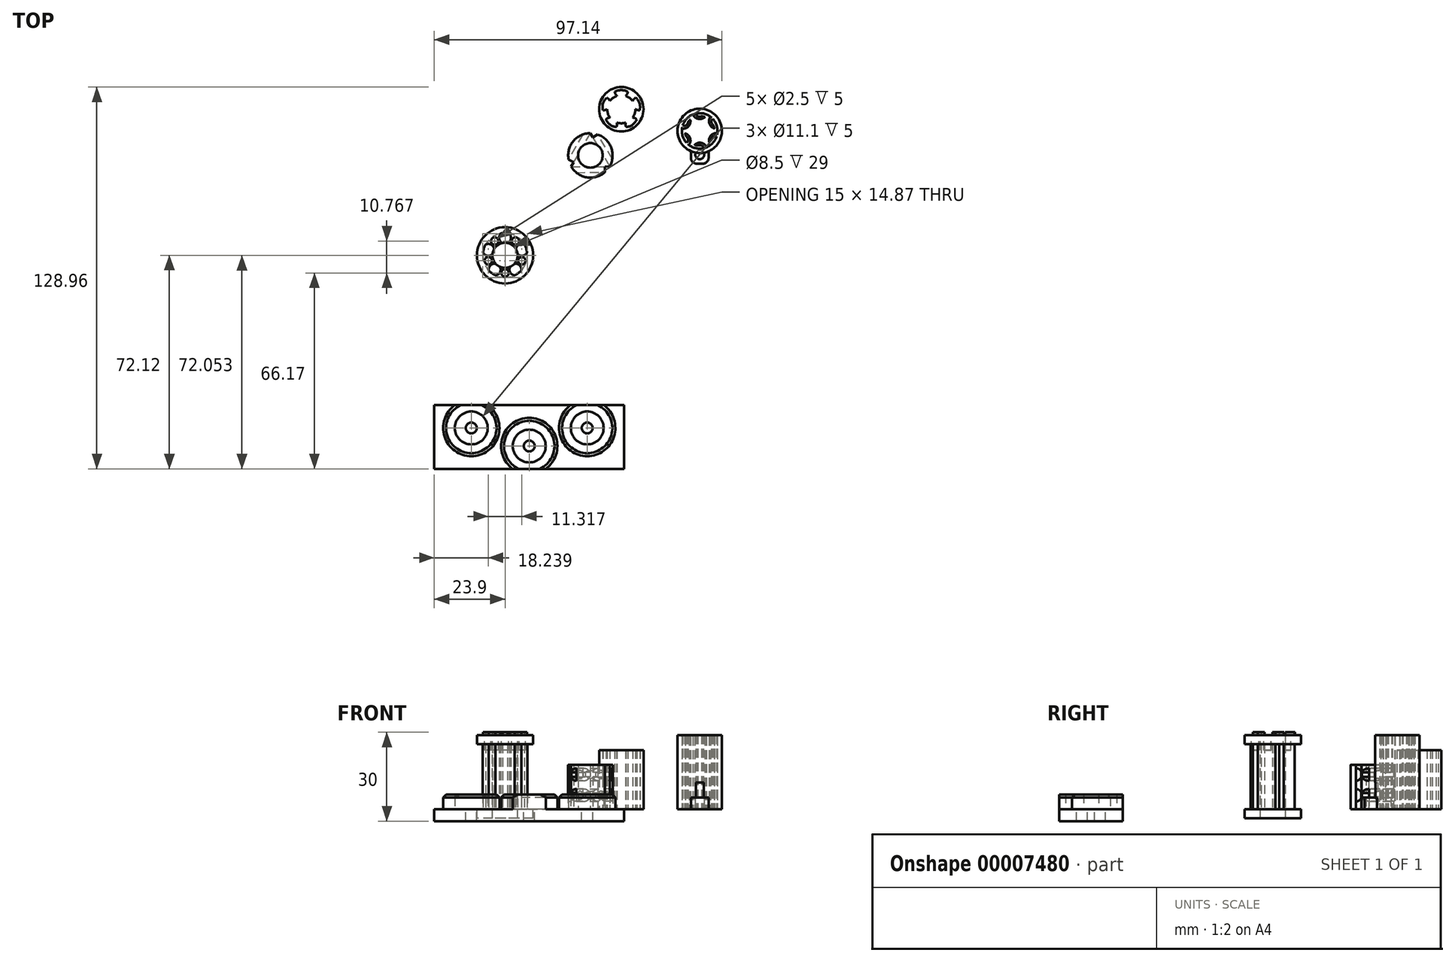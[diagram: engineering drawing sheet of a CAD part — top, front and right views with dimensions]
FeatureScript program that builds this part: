
annotation { "Feature Type Name" : "Feature", "Feature Type Description" : "" }
export const myFeature = defineFeature(function(context is Context, id is Id, definition is map)
    precondition{}
    {
        {
            var Q0;
            Q0=qCreatedBy(makeId("Top.planeOp"),FACE);
            var sketch = newSketch(context, id + "F0", { "sketchPlane" : qUnion([Q0])});
            skCircle(sketch, "E0", {"center": v(0, 0) * mm, "radius": 7.5 * mm});
            skCircle(sketch, "E1", {"center": v(0, 0) * mm, "radius": 3.95 * mm, "construction": true});
            skLineSegment(sketch, "E2", {"start": v(0, 3.95) * mm, "end": v(0, 7.5) * mm, "construction": true});
            skCircle(sketch, "E3", {"center": v(0, 5.95) * mm, "radius": 2 * mm});
            skCircle(sketch, "E4", {"center": v(0, 0) * mm, "radius": 4.25 * mm});
            skCircle(sketch, "E5", {"center": v(0, 0) * mm, "radius": 9.5 * mm});
            skCircle(sketch, "E6.1.0", {"center": v(-5.66, 1.84) * mm, "radius": 2 * mm});
            skCircle(sketch, "E6.2.0", {"center": v(-3.5, -4.81) * mm, "radius": 2 * mm});
            skCircle(sketch, "E6.3.0", {"center": v(3.5, -4.81) * mm, "radius": 2 * mm});
            skCircle(sketch, "E6.4.0", {"center": v(5.66, 1.84) * mm, "radius": 2 * mm});
            skSolve(sketch);
        }
        {
            var Q0;
            Q0=makeQuery(id+"F0.imprint","IMPRINT",FACE,{"disambiguationData":[TD([[makeQuery(id+"F0.imprint","IMPRINT",EDGE,{"derivedFrom":sQuery(id+"F0.wireOp",EDGE,"E5")}),1.0]])]});
            var Q1;
            {var subQ0=sQuery(id+"F0.wireOp",EDGE,"E6.4.0");var subQ3=sQuery(id+"F0.wireOp",EDGE,"E0");var subQ6=makeQuery(id+"F0.imprint","INTERSECT",VERTEX,{"disambiguationData":[OD(0.0)],"derivedFrom":[subQ3,subQ0]});Q1=makeQuery(id+"F0.imprint","IMPRINT",FACE,{"disambiguationData":[TD([[makeQuery(id+"F0.imprint","IMPRINT",EDGE,{"disambiguationData":[TD([[subQ6,1.0]])],"derivedFrom":subQ3}),1.0]])]});}
            var Q2;
            {var subQ3=sQuery(id+"F0.wireOp",EDGE,"E0");var subQ5=sQuery(id+"F0.wireOp",EDGE,"E6.1.0");var subQ7=makeQuery(id+"F0.imprint","INTERSECT",VERTEX,{"disambiguationData":[OD(1.0)],"derivedFrom":[subQ3,subQ5]});Q2=makeQuery(id+"F0.imprint","IMPRINT",FACE,{"disambiguationData":[TD([[makeQuery(id+"F0.imprint","IMPRINT",EDGE,{"disambiguationData":[TD([[subQ7,-1.0]])],"derivedFrom":subQ3}),1.0]])]});}
            var Q3;
            {var subQ3=sQuery(id+"F0.wireOp",EDGE,"E0");var subQ5=sQuery(id+"F0.wireOp",EDGE,"E3");var subQ7=makeQuery(id+"F0.imprint","INTERSECT",VERTEX,{"disambiguationData":[OD(1.0)],"derivedFrom":[subQ3,subQ5]});Q3=makeQuery(id+"F0.imprint","IMPRINT",FACE,{"disambiguationData":[TD([[makeQuery(id+"F0.imprint","IMPRINT",EDGE,{"disambiguationData":[TD([[subQ7,-1.0]])],"derivedFrom":subQ3}),1.0]])]});}
            var Q4;
            {var subQ1=sQuery(id+"F0.wireOp",EDGE,"E3");var subQ4=sQuery(id+"F0.wireOp",EDGE,"E0");var subQ5=makeQuery(id+"F0.imprint","INTERSECT",VERTEX,{"disambiguationData":[OD(0.0)],"derivedFrom":[subQ4,subQ1]});Q4=makeQuery(id+"F0.imprint","IMPRINT",FACE,{"disambiguationData":[TD([[makeQuery(id+"F0.imprint","IMPRINT",EDGE,{"disambiguationData":[TD([[subQ5,-1.0]])],"derivedFrom":subQ4}),1.0]])]});}
            var Q5;
            {var subQ0=sQuery(id+"F0.wireOp",EDGE,"E6.4.0");var subQ3=sQuery(id+"F0.wireOp",EDGE,"E0");var subQ4=makeQuery(id+"F0.imprint","INTERSECT",VERTEX,{"disambiguationData":[OD(0.0)],"derivedFrom":[subQ3,subQ0]});Q5=makeQuery(id+"F0.imprint","IMPRINT",FACE,{"disambiguationData":[TD([[makeQuery(id+"F0.imprint","IMPRINT",EDGE,{"disambiguationData":[TD([[subQ4,-1.0]])],"derivedFrom":subQ3}),1.0]])]});}
            var Q6;
            {var subQ0=sQuery(id+"F0.wireOp",EDGE,"E6.1.0");var subQ3=sQuery(id+"F0.wireOp",EDGE,"E0");var subQ4=makeQuery(id+"F0.imprint","INTERSECT",VERTEX,{"disambiguationData":[OD(0.0)],"derivedFrom":[subQ3,subQ0]});Q6=makeQuery(id+"F0.imprint","IMPRINT",FACE,{"disambiguationData":[TD([[makeQuery(id+"F0.imprint","IMPRINT",EDGE,{"disambiguationData":[TD([[subQ4,-1.0]])],"derivedFrom":subQ3}),1.0]])]});}
            var Q7;
            {var subQ0=sQuery(id+"F0.wireOp",EDGE,"E6.4.0");var subQ1=sQuery(id+"F0.wireOp",EDGE,"E0");var subQ3=makeQuery(id+"F0.imprint","INTERSECT",VERTEX,{"disambiguationData":[OD(0.0)],"derivedFrom":[subQ1,subQ0]});Q7=makeQuery(id+"F0.imprint","IMPRINT",FACE,{"disambiguationData":[TD([[makeQuery(id+"F0.imprint","IMPRINT",EDGE,{"disambiguationData":[TD([[subQ3,1.0]])],"derivedFrom":subQ1}),-1.0]])]});}
            var Q8;
            {var subQ0=sQuery(id+"F0.wireOp",EDGE,"E6.1.0");var subQ1=sQuery(id+"F0.wireOp",EDGE,"E0");var subQ3=makeQuery(id+"F0.imprint","INTERSECT",VERTEX,{"disambiguationData":[OD(0.0)],"derivedFrom":[subQ1,subQ0]});Q8=makeQuery(id+"F0.imprint","IMPRINT",FACE,{"disambiguationData":[TD([[makeQuery(id+"F0.imprint","IMPRINT",EDGE,{"disambiguationData":[TD([[subQ3,-1.0]])],"derivedFrom":subQ1}),-1.0]])]});}
            var Q9;
            {var subQ0=sQuery(id+"F0.wireOp",EDGE,"E3");var subQ1=sQuery(id+"F0.wireOp",EDGE,"E0");var subQ3=makeQuery(id+"F0.imprint","INTERSECT",VERTEX,{"disambiguationData":[OD(0.0)],"derivedFrom":[subQ1,subQ0]});Q9=makeQuery(id+"F0.imprint","IMPRINT",FACE,{"disambiguationData":[TD([[makeQuery(id+"F0.imprint","IMPRINT",EDGE,{"disambiguationData":[TD([[subQ3,-1.0]])],"derivedFrom":subQ1}),-1.0]])]});}
            var Q10;
            {var subQ0=sQuery(id+"F0.wireOp",EDGE,"E6.3.0");var subQ1=sQuery(id+"F0.wireOp",EDGE,"E0");var subQ3=makeQuery(id+"F0.imprint","INTERSECT",VERTEX,{"disambiguationData":[OD(0.0)],"derivedFrom":[subQ1,subQ0]});Q10=makeQuery(id+"F0.imprint","IMPRINT",FACE,{"disambiguationData":[TD([[makeQuery(id+"F0.imprint","IMPRINT",EDGE,{"disambiguationData":[TD([[subQ3,-1.0]])],"derivedFrom":subQ1}),-1.0]])]});}
            var Q11;
            {var subQ0=sQuery(id+"F0.wireOp",EDGE,"E6.4.0");var subQ3=sQuery(id+"F0.wireOp",EDGE,"E0");var subQ4=makeQuery(id+"F0.imprint","INTERSECT",VERTEX,{"disambiguationData":[OD(1.0)],"derivedFrom":[subQ3,subQ0]});Q11=makeQuery(id+"F0.imprint","IMPRINT",FACE,{"disambiguationData":[TD([[makeQuery(id+"F0.imprint","IMPRINT",EDGE,{"disambiguationData":[TD([[subQ4,1.0]])],"derivedFrom":subQ3}),1.0]])]});}
            var Q12;
            {var subQ0=sQuery(id+"F0.wireOp",EDGE,"E6.2.0");var subQ1=sQuery(id+"F0.wireOp",EDGE,"E0");var subQ3=makeQuery(id+"F0.imprint","INTERSECT",VERTEX,{"disambiguationData":[OD(0.0)],"derivedFrom":[subQ1,subQ0]});Q12=makeQuery(id+"F0.imprint","IMPRINT",FACE,{"disambiguationData":[TD([[makeQuery(id+"F0.imprint","IMPRINT",EDGE,{"disambiguationData":[TD([[subQ3,-1.0]])],"derivedFrom":subQ1}),-1.0]])]});}
            var Q13;
            {var subQ3=sQuery(id+"F0.wireOp",EDGE,"E0");var subQ5=sQuery(id+"F0.wireOp",EDGE,"E6.2.0");var subQ7=makeQuery(id+"F0.imprint","INTERSECT",VERTEX,{"disambiguationData":[OD(1.0)],"derivedFrom":[subQ3,subQ5]});Q13=makeQuery(id+"F0.imprint","IMPRINT",FACE,{"disambiguationData":[TD([[makeQuery(id+"F0.imprint","IMPRINT",EDGE,{"disambiguationData":[TD([[subQ7,-1.0]])],"derivedFrom":subQ3}),1.0]])]});}
            var Q14;
            {var subQ0=sQuery(id+"F0.wireOp",EDGE,"E6.2.0");var subQ3=sQuery(id+"F0.wireOp",EDGE,"E0");var subQ4=makeQuery(id+"F0.imprint","INTERSECT",VERTEX,{"disambiguationData":[OD(0.0)],"derivedFrom":[subQ3,subQ0]});Q14=makeQuery(id+"F0.imprint","IMPRINT",FACE,{"disambiguationData":[TD([[makeQuery(id+"F0.imprint","IMPRINT",EDGE,{"disambiguationData":[TD([[subQ4,-1.0]])],"derivedFrom":subQ3}),1.0]])]});}
            var Q15;
            {var subQ0=sQuery(id+"F0.wireOp",EDGE,"E6.3.0");var subQ3=sQuery(id+"F0.wireOp",EDGE,"E0");var subQ4=makeQuery(id+"F0.imprint","INTERSECT",VERTEX,{"disambiguationData":[OD(0.0)],"derivedFrom":[subQ3,subQ0]});Q15=makeQuery(id+"F0.imprint","IMPRINT",FACE,{"disambiguationData":[TD([[makeQuery(id+"F0.imprint","IMPRINT",EDGE,{"disambiguationData":[TD([[subQ4,-1.0]])],"derivedFrom":subQ3}),1.0]])]});}
            extrude(context, id + "F1", {"entities" : qUnion([Q0, Q1, Q2, Q3, Q4, Q5, Q6, Q7, Q8, Q9, Q10, Q11, Q12, Q13, Q14, Q15]), "oppositeDirection" : true, "depth" : 3 * mm});
        }
        {
            var Q0;
            {var subQ3=sQuery(id+"F0.wireOp",EDGE,"E0");var subQ5=sQuery(id+"F0.wireOp",EDGE,"E3");var subQ7=makeQuery(id+"F0.imprint","INTERSECT",VERTEX,{"disambiguationData":[OD(1.0)],"derivedFrom":[subQ3,subQ5]});Q0=makeQuery(id+"F0.imprint","IMPRINT",FACE,{"disambiguationData":[TD([[makeQuery(id+"F0.imprint","IMPRINT",EDGE,{"disambiguationData":[TD([[subQ7,-1.0]])],"derivedFrom":subQ3}),1.0]])]});}
            var Q1;
            {var subQ3=sQuery(id+"F0.wireOp",EDGE,"E0");var subQ5=sQuery(id+"F0.wireOp",EDGE,"E6.1.0");var subQ7=makeQuery(id+"F0.imprint","INTERSECT",VERTEX,{"disambiguationData":[OD(1.0)],"derivedFrom":[subQ3,subQ5]});Q1=makeQuery(id+"F0.imprint","IMPRINT",FACE,{"disambiguationData":[TD([[makeQuery(id+"F0.imprint","IMPRINT",EDGE,{"disambiguationData":[TD([[subQ7,-1.0]])],"derivedFrom":subQ3}),1.0]])]});}
            var Q2;
            {var subQ3=sQuery(id+"F0.wireOp",EDGE,"E0");var subQ5=sQuery(id+"F0.wireOp",EDGE,"E6.2.0");var subQ7=makeQuery(id+"F0.imprint","INTERSECT",VERTEX,{"disambiguationData":[OD(1.0)],"derivedFrom":[subQ3,subQ5]});Q2=makeQuery(id+"F0.imprint","IMPRINT",FACE,{"disambiguationData":[TD([[makeQuery(id+"F0.imprint","IMPRINT",EDGE,{"disambiguationData":[TD([[subQ7,-1.0]])],"derivedFrom":subQ3}),1.0]])]});}
            var Q3;
            {var subQ0=sQuery(id+"F0.wireOp",EDGE,"E6.4.0");var subQ3=sQuery(id+"F0.wireOp",EDGE,"E0");var subQ4=makeQuery(id+"F0.imprint","INTERSECT",VERTEX,{"disambiguationData":[OD(1.0)],"derivedFrom":[subQ3,subQ0]});Q3=makeQuery(id+"F0.imprint","IMPRINT",FACE,{"disambiguationData":[TD([[makeQuery(id+"F0.imprint","IMPRINT",EDGE,{"disambiguationData":[TD([[subQ4,1.0]])],"derivedFrom":subQ3}),1.0]])]});}
            var Q4;
            {var subQ0=sQuery(id+"F0.wireOp",EDGE,"E6.4.0");var subQ3=sQuery(id+"F0.wireOp",EDGE,"E0");var subQ4=makeQuery(id+"F0.imprint","INTERSECT",VERTEX,{"disambiguationData":[OD(0.0)],"derivedFrom":[subQ3,subQ0]});Q4=makeQuery(id+"F0.imprint","IMPRINT",FACE,{"disambiguationData":[TD([[makeQuery(id+"F0.imprint","IMPRINT",EDGE,{"disambiguationData":[TD([[subQ4,-1.0]])],"derivedFrom":subQ3}),1.0]])]});}
            extrude(context, id + "F2", {"entities" : qUnion([Q0, Q1, Q2, Q3, Q4]), "operationType" : NewBodyOperationType.ADD, "depth" : 22 * mm});
        }
        {
            var Q0;
            Q0=makeQuery(id+"F2.opExtrude","CAP_FACE",FACE,{"disambiguationData":[OSD([sQuery(id+"F0.wireOp",EDGE,"E0"),sQuery(id+"F0.wireOp",EDGE,"E3"),sQuery(id+"F0.wireOp",EDGE,"E4"),sQuery(id+"F0.wireOp",EDGE,"E6.1.0")])],"isStart":false});
            var sketch = newSketch(context, id + "F3", { "sketchPlane" : qUnion([Q0])});
            skCircle(sketch, "E7.0", {"center": v(0, 0) * mm, "radius": 7.5 * mm});
            skCircle(sketch, "E8.0", {"center": v(0, 0) * mm, "radius": 9.5 * mm});
            skCircle(sketch, "E9.0", {"center": v(0, 0) * mm, "radius": 4.25 * mm});
            skArc(sketch, "E10.0", {"start": v(-3.68, 2.13) * mm, "mid": v(-4.74, 3.62) * mm, "end": v(-6.57, 3.62) * mm});
            skArc(sketch, "E11.0", {"start": v(-7.44, 0.93) * mm, "mid": v(-5.96, -0.14) * mm, "end": v(-4.23, 0.44) * mm});
            skArc(sketch, "E12.0", {"start": v(-3.16, -2.84) * mm, "mid": v(-4.9, -3.4) * mm, "end": v(-5.47, -5.13) * mm});
            skArc(sketch, "E13.0", {"start": v(-3.19, -6.79) * mm, "mid": v(-1.71, -5.71) * mm, "end": v(-1.73, -3.88) * mm});
            skArc(sketch, "E14.0", {"start": v(1.73, -3.88) * mm, "mid": v(1.71, -5.71) * mm, "end": v(3.19, -6.79) * mm});
            skArc(sketch, "E15.0", {"start": v(5.47, -5.13) * mm, "mid": v(4.9, -3.4) * mm, "end": v(3.16, -2.84) * mm});
            skArc(sketch, "E16.0", {"start": v(4.23, 0.44) * mm, "mid": v(5.96, -0.14) * mm, "end": v(7.44, 0.93) * mm});
            skArc(sketch, "E17.0", {"start": v(6.57, 3.62) * mm, "mid": v(4.74, 3.62) * mm, "end": v(3.68, 2.13) * mm});
            skArc(sketch, "E18.0", {"start": v(0.89, 4.16) * mm, "mid": v(1.97, 5.63) * mm, "end": v(1.41, 7.37) * mm});
            skArc(sketch, "E19.0", {"start": v(-1.41, 7.37) * mm, "mid": v(-1.97, 5.63) * mm, "end": v(-0.89, 4.16) * mm});
            skSolve(sketch);
        }
        {
            var Q0;
            Q0=makeQuery(id+"F3.imprint","IMPRINT",FACE,{"disambiguationData":[TD([[makeQuery(id+"F3.imprint","IMPRINT",EDGE,{"derivedFrom":sQuery(id+"F3.wireOp",EDGE,"E8.0")}),1.0]])]});
            var Q1;
            {var subQ1=sQuery(id+"F3.wireOp",EDGE,"E17.0");Q1=makeQuery(id+"F3.imprint","IMPRINT",FACE,{"disambiguationData":[TD([[makeQuery(id+"F3.imprint","IMPRINT",EDGE,{"derivedFrom":subQ1}),-1.0]])]});}
            var Q2;
            {var subQ1=sQuery(id+"F3.wireOp",EDGE,"E10.0");Q2=makeQuery(id+"F3.imprint","IMPRINT",FACE,{"disambiguationData":[TD([[makeQuery(id+"F3.imprint","IMPRINT",EDGE,{"derivedFrom":subQ1}),-1.0]])]});}
            var Q3;
            {var subQ1=sQuery(id+"F3.wireOp",EDGE,"E15.0");Q3=makeQuery(id+"F3.imprint","IMPRINT",FACE,{"disambiguationData":[TD([[makeQuery(id+"F3.imprint","IMPRINT",EDGE,{"derivedFrom":subQ1}),-1.0]])]});}
            var Q4;
            {var subQ1=sQuery(id+"F3.wireOp",EDGE,"E13.0");Q4=makeQuery(id+"F3.imprint","IMPRINT",FACE,{"disambiguationData":[TD([[makeQuery(id+"F3.imprint","IMPRINT",EDGE,{"derivedFrom":subQ1}),-1.0]])]});}
            var Q5;
            {var subQ1=sQuery(id+"F3.wireOp",EDGE,"E11.0");Q5=makeQuery(id+"F3.imprint","IMPRINT",FACE,{"disambiguationData":[TD([[makeQuery(id+"F3.imprint","IMPRINT",EDGE,{"derivedFrom":subQ1}),-1.0]])]});}
            extrude(context, id + "F4", {"entities" : qUnion([Q0, Q1, Q2, Q3, Q4, Q5]), "depth" : 3 * mm});
        }
        {
            var Q0;
            {var subQ1=sQuery(id+"F3.wireOp",EDGE,"E18.0");Q0=makeQuery(id+"F3.imprint","IMPRINT",FACE,{"disambiguationData":[TD([[makeQuery(id+"F3.imprint","IMPRINT",EDGE,{"derivedFrom":subQ1}),1.0]])]});}
            var Q1;
            {var subQ0=sQuery(id+"F3.wireOp",EDGE,"E10.0");Q1=makeQuery(id+"F3.imprint","IMPRINT",FACE,{"disambiguationData":[TD([[makeQuery(id+"F3.imprint","IMPRINT",EDGE,{"derivedFrom":subQ0}),1.0]])]});}
            var Q2;
            {var subQ1=sQuery(id+"F3.wireOp",EDGE,"E12.0");Q2=makeQuery(id+"F3.imprint","IMPRINT",FACE,{"disambiguationData":[TD([[makeQuery(id+"F3.imprint","IMPRINT",EDGE,{"derivedFrom":subQ1}),1.0]])]});}
            var Q3;
            {var subQ1=sQuery(id+"F3.wireOp",EDGE,"E14.0");Q3=makeQuery(id+"F3.imprint","IMPRINT",FACE,{"disambiguationData":[TD([[makeQuery(id+"F3.imprint","IMPRINT",EDGE,{"derivedFrom":subQ1}),1.0]])]});}
            var Q4;
            {var subQ1=sQuery(id+"F3.wireOp",EDGE,"E16.0");Q4=makeQuery(id+"F3.imprint","IMPRINT",FACE,{"disambiguationData":[TD([[makeQuery(id+"F3.imprint","IMPRINT",EDGE,{"derivedFrom":subQ1}),1.0]])]});}
            extrude(context, id + "F5", {"entities" : qUnion([Q0, Q1, Q2, Q3, Q4]), "operationType" : NewBodyOperationType.ADD, "depth" : 4 * mm});
        }
        {
            var Q0;
            Q0=makeQuery(id+"F4.opExtrude","CAP_FACE",FACE,{"disambiguationData":[OSD([sQuery(id+"F3.wireOp",EDGE,"E7.0"),sQuery(id+"F3.wireOp",EDGE,"E8.0"),sQuery(id+"F3.wireOp",EDGE,"E9.0"),sQuery(id+"F3.wireOp",EDGE,"E10.0"),sQuery(id+"F3.wireOp",EDGE,"E11.0"),sQuery(id+"F3.wireOp",EDGE,"E12.0"),sQuery(id+"F3.wireOp",EDGE,"E13.0"),sQuery(id+"F3.wireOp",EDGE,"E14.0"),sQuery(id+"F3.wireOp",EDGE,"E15.0"),sQuery(id+"F3.wireOp",EDGE,"E16.0"),sQuery(id+"F3.wireOp",EDGE,"E17.0"),sQuery(id+"F3.wireOp",EDGE,"E18.0"),sQuery(id+"F3.wireOp",EDGE,"E19.0")])],"isStart":false});
            var sketch = newSketch(context, id + "F6", { "sketchPlane" : qUnion([Q0])});
            skCircle(sketch, "E20", {"center": v(0, 0) * mm, "radius": 5.95 * mm, "construction": true});
            skCircle(sketch, "E21", {"center": v(-3.5, 4.82) * mm, "radius": 1.25 * mm});
            skCircle(sketch, "E22.1.0", {"center": v(-5.66, -1.83) * mm, "radius": 1.25 * mm});
            skCircle(sketch, "E22.2.0", {"center": v(0, -5.95) * mm, "radius": 1.25 * mm});
            skCircle(sketch, "E22.3.0", {"center": v(5.66, -1.84) * mm, "radius": 1.25 * mm});
            skCircle(sketch, "E22.4.0", {"center": v(3.5, 4.81) * mm, "radius": 1.25 * mm});
            skSolve(sketch);
        }
        {
            var Q0;
            Q0=makeQuery(id+"F6.imprint","IMPRINT",FACE,{"disambiguationData":[TD([[makeQuery(id+"F6.imprint","IMPRINT",EDGE,{"derivedFrom":sQuery(id+"F6.wireOp",EDGE,"E21")}),1.0]])]});
            var Q1;
            Q1=makeQuery(id+"F6.imprint","IMPRINT",FACE,{"disambiguationData":[TD([[makeQuery(id+"F6.imprint","IMPRINT",EDGE,{"derivedFrom":sQuery(id+"F6.wireOp",EDGE,"E22.1.0")}),1.0]])]});
            var Q2;
            Q2=makeQuery(id+"F6.imprint","IMPRINT",FACE,{"disambiguationData":[TD([[makeQuery(id+"F6.imprint","IMPRINT",EDGE,{"derivedFrom":sQuery(id+"F6.wireOp",EDGE,"E22.2.0")}),1.0]])]});
            var Q3;
            Q3=makeQuery(id+"F6.imprint","IMPRINT",FACE,{"disambiguationData":[TD([[makeQuery(id+"F6.imprint","IMPRINT",EDGE,{"derivedFrom":sQuery(id+"F6.wireOp",EDGE,"E22.3.0")}),1.0]])]});
            var Q4;
            Q4=makeQuery(id+"F6.imprint","IMPRINT",FACE,{"disambiguationData":[TD([[makeQuery(id+"F6.imprint","IMPRINT",EDGE,{"derivedFrom":sQuery(id+"F6.wireOp",EDGE,"E22.4.0")}),1.0]])]});
            extrude(context, id + "F7", {"entities" : qUnion([Q0, Q1, Q2, Q3, Q4]), "operationType" : NewBodyOperationType.REMOVE, "oppositeDirection" : true, "depth" : 5 * mm});
        }
        {
            var Q0;
            Q0=qCreatedBy(makeId("Top.planeOp"),FACE);
            var sketch = newSketch(context, id + "F8", { "sketchPlane" : qUnion([Q0])});
            skLineSegment(sketch, "E23.bottom", {"start": v(-23.9, -50.62) * mm, "end": v(40.24, -50.62) * mm});
            skLineSegment(sketch, "E23.top", {"start": v(-23.9, -72.12) * mm, "end": v(40.24, -72.12) * mm});
            skLineSegment(sketch, "E23.left", {"start": v(-23.9, -50.62) * mm, "end": v(-23.9, -72.12) * mm});
            skLineSegment(sketch, "E23.right", {"start": v(40.24, -50.62) * mm, "end": v(40.24, -72.12) * mm});
            skLineSegment(sketch, "E24.0", {"start": v(-26.4, -48.12) * mm, "end": v(42.74, -48.12) * mm});
            skLineSegment(sketch, "E24.1", {"start": v(-26.4, -48.12) * mm, "end": v(-26.4, -74.62) * mm});
            skLineSegment(sketch, "E24.2", {"start": v(-26.4, -74.62) * mm, "end": v(42.74, -74.62) * mm});
            skLineSegment(sketch, "E24.3", {"start": v(42.74, -48.12) * mm, "end": v(42.74, -74.62) * mm});
            skLineSegment(sketch, "E25.0", {"start": v(-25.7, -48.82) * mm, "end": v(42.04, -48.82) * mm, "construction": true});
            skLineSegment(sketch, "E25.1", {"start": v(-25.7, -48.82) * mm, "end": v(-25.7, -73.92) * mm, "construction": true});
            skLineSegment(sketch, "E25.2", {"start": v(-25.7, -73.92) * mm, "end": v(42.04, -73.92) * mm, "construction": true});
            skLineSegment(sketch, "E25.3", {"start": v(42.04, -48.82) * mm, "end": v(42.04, -73.92) * mm, "construction": true});
            skCircle(sketch, "E26", {"center": v(-11.4, -58.32) * mm, "radius": 9.5 * mm});
            skCircle(sketch, "E27", {"center": v(8.17, -64.42) * mm, "radius": 9.5 * mm});
            skCircle(sketch, "E28", {"center": v(27.74, -58.32) * mm, "radius": 9.5 * mm});
            skCircle(sketch, "E29", {"center": v(-11.4, -58.32) * mm, "radius": 5.55 * mm});
            skCircle(sketch, "E30", {"center": v(8.17, -64.42) * mm, "radius": 5.55 * mm});
            skCircle(sketch, "E31", {"center": v(27.74, -58.32) * mm, "radius": 5.55 * mm});
            skCircle(sketch, "E32", {"center": v(-11.4, -58.32) * mm, "radius": 1.85 * mm});
            skCircle(sketch, "E33", {"center": v(8.17, -64.42) * mm, "radius": 1.85 * mm});
            skCircle(sketch, "E34", {"center": v(27.74, -58.32) * mm, "radius": 1.85 * mm});
            skSolve(sketch);
        }
        {
            var Q0;
            Q0=makeQuery(id+"F8.imprint","IMPRINT",FACE,{"disambiguationData":[TD([[makeQuery(id+"F8.imprint","IMPRINT",EDGE,{"derivedFrom":sQuery(id+"F8.wireOp",EDGE,"E23.bottom")}),-1.0]])]});
            var Q1;
            Q1=makeQuery(id+"F8.imprint","IMPRINT",FACE,{"disambiguationData":[TD([[makeQuery(id+"F8.imprint","IMPRINT",EDGE,{"derivedFrom":sQuery(id+"F8.wireOp",EDGE,"E29")}),1.0]])]});
            var Q2;
            Q2=makeQuery(id+"F8.imprint","IMPRINT",FACE,{"disambiguationData":[TD([[makeQuery(id+"F8.imprint","IMPRINT",EDGE,{"derivedFrom":sQuery(id+"F8.wireOp",EDGE,"E30")}),1.0]])]});
            var Q3;
            Q3=makeQuery(id+"F8.imprint","IMPRINT",FACE,{"disambiguationData":[TD([[makeQuery(id+"F8.imprint","IMPRINT",EDGE,{"derivedFrom":sQuery(id+"F8.wireOp",EDGE,"E31")}),1.0]])]});
            var Q4;
            Q4=makeQuery(id+"F8.imprint","IMPRINT",FACE,{"disambiguationData":[TD([[makeQuery(id+"F8.imprint","IMPRINT",EDGE,{"derivedFrom":sQuery(id+"F8.wireOp",EDGE,"E29")}),-1.0]])]});
            var Q5;
            Q5=makeQuery(id+"F8.imprint","IMPRINT",FACE,{"disambiguationData":[TD([[makeQuery(id+"F8.imprint","IMPRINT",EDGE,{"derivedFrom":sQuery(id+"F8.wireOp",EDGE,"E30")}),-1.0]])]});
            var Q6;
            Q6=makeQuery(id+"F8.imprint","IMPRINT",FACE,{"disambiguationData":[TD([[makeQuery(id+"F8.imprint","IMPRINT",EDGE,{"derivedFrom":sQuery(id+"F8.wireOp",EDGE,"E31")}),-1.0]])]});
            extrude(context, id + "F9", {"entities" : qUnion([Q0, Q1, Q2, Q3, Q4, Q5, Q6]), "oppositeDirection" : true, "depth" : 4 * mm});
        }
        {
            var Q0;
            Q0=makeQuery(id+"F8.imprint","IMPRINT",FACE,{"disambiguationData":[TD([[makeQuery(id+"F8.imprint","IMPRINT",EDGE,{"derivedFrom":sQuery(id+"F8.wireOp",EDGE,"E29")}),-1.0]])]});
            var Q1;
            Q1=makeQuery(id+"F8.imprint","IMPRINT",FACE,{"disambiguationData":[TD([[makeQuery(id+"F8.imprint","IMPRINT",EDGE,{"derivedFrom":sQuery(id+"F8.wireOp",EDGE,"E30")}),-1.0]])]});
            var Q2;
            Q2=makeQuery(id+"F8.imprint","IMPRINT",FACE,{"disambiguationData":[TD([[makeQuery(id+"F8.imprint","IMPRINT",EDGE,{"derivedFrom":sQuery(id+"F8.wireOp",EDGE,"E31")}),-1.0]])]});
            extrude(context, id + "F10", {"entities" : qUnion([Q0, Q1, Q2]), "operationType" : NewBodyOperationType.ADD, "depth" : 5 * mm});
        }
        {
            var Q0;
            Q0=makeQuery(id+"F10.opExtrude","CAP_EDGE",EDGE,{"disambiguationData":[OSD([sQuery(id+"F8.wireOp",EDGE,"E26")])],"isStart":false});
            var Q1;
            Q1=makeQuery(id+"F10.opExtrude","CAP_EDGE",EDGE,{"disambiguationData":[OSD([sQuery(id+"F8.wireOp",EDGE,"E27")])],"isStart":false});
            var Q2;
            Q2=makeQuery(id+"F10.opExtrude","CAP_EDGE",EDGE,{"disambiguationData":[OSD([sQuery(id+"F8.wireOp",EDGE,"E28")])],"isStart":false});
            chamfer(context, id + "F11", {"entities" : qUnion([Q0, Q1, Q2]), "width" : 1 * mm, "tangentPropagation" : true});
        }
        {
            var Q0;
            Q0=qCreatedBy(makeId("Top.planeOp"),FACE);
            var sketch = newSketch(context, id + "F12", { "sketchPlane" : qUnion([Q0])});
            skCircle(sketch, "E35", {"center": v(28.82, 33.75) * mm, "radius": 7.5 * mm});
            skCircle(sketch, "E36", {"center": v(28.82, 33.75) * mm, "radius": 4.15 * mm});
            skLineSegment(sketch, "E37", {"start": v(31.33, 40.82) * mm, "end": v(36.22, 32.52) * mm, "construction": true});
            skCircle(sketch, "E38", {"center": v(28.82, 33.75) * mm, "radius": 3.75 * mm, "construction": true});
            skLineSegment(sketch, "E39", {"start": v(31.33, 40.82) * mm, "end": v(29.65, 39.83) * mm});
            skLineSegment(sketch, "E40", {"start": v(29.65, 39.83) * mm, "end": v(28.81, 41.25) * mm});
            skLineSegment(sketch, "E41.1.0", {"start": v(23.14, 31.43) * mm, "end": v(22.33, 30) * mm});
            skLineSegment(sketch, "E41.1.1", {"start": v(21.44, 32.4) * mm, "end": v(23.14, 31.43) * mm});
            skLineSegment(sketch, "E41.1.2", {"start": v(21.44, 32.4) * mm, "end": v(26.19, 40.77) * mm, "construction": true});
            skLineSegment(sketch, "E41.2.0", {"start": v(33.67, 30) * mm, "end": v(35.32, 30) * mm});
            skLineSegment(sketch, "E41.2.1", {"start": v(33.68, 28.04) * mm, "end": v(33.67, 30) * mm});
            skLineSegment(sketch, "E41.2.2", {"start": v(33.68, 28.04) * mm, "end": v(24.05, 27.96) * mm, "construction": true});
            skCircle(sketch, "E42", {"center": v(39.25, 49.34) * mm, "radius": 4.75 * mm});
            skCircle(sketch, "E43", {"center": v(39.25, 49.34) * mm, "radius": 7.5 * mm});
            skCircle(sketch, "E44", {"center": v(39.25, 49.34) * mm, "radius": 4 * mm, "construction": true});
            skLineSegment(sketch, "E45", {"start": v(39.25, 49.34) * mm, "end": v(39.25, 56.84) * mm, "construction": true});
            skArc(sketch, "E46", {"start": v(37.04, 55.16) * mm, "mid": v(39.25, 53.34) * mm, "end": v(41.46, 55.16) * mm});
            skArc(sketch, "E47", {"start": v(41.46, 55.16) * mm, "mid": v(39.25, 55.82) * mm, "end": v(37.04, 55.16) * mm});
            skLineSegment(sketch, "E48", {"start": v(37.04, 55.16) * mm, "end": v(41.46, 55.16) * mm, "construction": true});
            skArc(sketch, "E49.1.0", {"start": v(34.4, 53.24) * mm, "mid": v(33.1, 51.34) * mm, "end": v(33.04, 49.04) * mm});
            skArc(sketch, "E49.1.1", {"start": v(33.04, 49.04) * mm, "mid": v(35.45, 50.58) * mm, "end": v(34.4, 53.24) * mm});
            skArc(sketch, "E49.2.0", {"start": v(34.05, 45.93) * mm, "mid": v(35.45, 44.1) * mm, "end": v(37.62, 43.34) * mm});
            skArc(sketch, "E49.2.1", {"start": v(37.62, 43.34) * mm, "mid": v(36.9, 46.1) * mm, "end": v(34.05, 45.93) * mm});
            skArc(sketch, "E49.3.0", {"start": v(40.89, 43.34) * mm, "mid": v(43.06, 44.1) * mm, "end": v(44.46, 45.93) * mm});
            skArc(sketch, "E49.3.1", {"start": v(44.46, 45.93) * mm, "mid": v(41.6, 46.1) * mm, "end": v(40.89, 43.34) * mm});
            skArc(sketch, "E49.4.0", {"start": v(45.47, 49.04) * mm, "mid": v(45.41, 51.34) * mm, "end": v(44.1, 53.24) * mm});
            skArc(sketch, "E49.4.1", {"start": v(44.1, 53.24) * mm, "mid": v(43.06, 50.58) * mm, "end": v(45.47, 49.04) * mm});
            skCircle(sketch, "E50", {"center": v(65.74, 42.03) * mm, "radius": 4 * mm, "construction": true});
            skCircle(sketch, "E51", {"center": v(65.74, 42.03) * mm, "radius": 7.5 * mm});
            skCircle(sketch, "E52", {"center": v(65.74, 42.03) * mm, "radius": 6 * mm});
            skLineSegment(sketch, "E53", {"start": v(65.74, 42.03) * mm, "end": v(65.74, 49.53) * mm, "construction": true});
            skArc(sketch, "E54", {"start": v(63.42, 47.57) * mm, "mid": v(65.2, 46.1) * mm, "end": v(67.45, 46.7) * mm});
            skArc(sketch, "E55.0", {"start": v(64.65, 47.22) * mm, "mid": v(65.48, 46.85) * mm, "end": v(66.38, 46.96) * mm});
            skArc(sketch, "E56", {"start": v(67.45, 46.7) * mm, "mid": v(66.92, 46.86) * mm, "end": v(66.38, 46.96) * mm});
            skLineSegment(sketch, "E57", {"start": v(64.5, 47.9) * mm, "end": v(64.65, 47.22) * mm});
            skLineSegment(sketch, "E58.1.0", {"start": v(60.04, 43.9) * mm, "end": v(60.7, 43.68) * mm});
            skArc(sketch, "E58.1.1", {"start": v(60.7, 43.68) * mm, "mid": v(61.44, 44.22) * mm, "end": v(61.8, 45.05) * mm});
            skArc(sketch, "E58.1.2", {"start": v(62.56, 45.84) * mm, "mid": v(62.16, 45.47) * mm, "end": v(61.8, 45.05) * mm});
            skArc(sketch, "E58.1.3", {"start": v(59.79, 42.79) * mm, "mid": v(61.96, 43.6) * mm, "end": v(62.56, 45.84) * mm});
            skLineSegment(sketch, "E58.2.0", {"start": v(61.27, 38.03) * mm, "end": v(61.8, 38.5) * mm});
            skArc(sketch, "E58.2.1", {"start": v(61.8, 38.5) * mm, "mid": v(61.7, 39.4) * mm, "end": v(61.16, 40.13) * mm});
            skArc(sketch, "E58.2.2", {"start": v(60.85, 41.18) * mm, "mid": v(60.97, 40.65) * mm, "end": v(61.16, 40.13) * mm});
            skArc(sketch, "E58.2.3", {"start": v(62.11, 37.26) * mm, "mid": v(62.5, 39.54) * mm, "end": v(60.85, 41.18) * mm});
            skLineSegment(sketch, "E58.3.0", {"start": v(66.98, 36.16) * mm, "end": v(66.83, 36.85) * mm});
            skArc(sketch, "E58.3.1", {"start": v(66.83, 36.85) * mm, "mid": v(66, 37.21) * mm, "end": v(65.1, 37.1) * mm});
            skArc(sketch, "E58.3.2", {"start": v(64.03, 37.37) * mm, "mid": v(64.56, 37.21) * mm, "end": v(65.1, 37.1) * mm});
            skArc(sketch, "E58.3.3", {"start": v(68.06, 36.5) * mm, "mid": v(66.27, 37.98) * mm, "end": v(64.03, 37.37) * mm});
            skLineSegment(sketch, "E58.4.0", {"start": v(71.44, 40.17) * mm, "end": v(70.78, 40.38) * mm});
            skArc(sketch, "E58.4.1", {"start": v(70.78, 40.38) * mm, "mid": v(70.05, 39.85) * mm, "end": v(69.68, 39.01) * mm});
            skArc(sketch, "E58.4.2", {"start": v(68.93, 38.22) * mm, "mid": v(69.33, 38.6) * mm, "end": v(69.68, 39.01) * mm});
            skArc(sketch, "E58.4.3", {"start": v(71.7, 41.28) * mm, "mid": v(69.52, 40.47) * mm, "end": v(68.93, 38.22) * mm});
            skLineSegment(sketch, "E58.5.0", {"start": v(70.2, 46.04) * mm, "end": v(69.69, 45.57) * mm});
            skArc(sketch, "E58.5.1", {"start": v(69.69, 45.57) * mm, "mid": v(69.79, 44.67) * mm, "end": v(70.33, 43.94) * mm});
            skArc(sketch, "E58.5.2", {"start": v(70.63, 42.89) * mm, "mid": v(70.5, 43.42) * mm, "end": v(70.33, 43.94) * mm});
            skArc(sketch, "E58.5.3", {"start": v(69.37, 46.81) * mm, "mid": v(68.99, 44.52) * mm, "end": v(70.63, 42.89) * mm});
            skSolve(sketch);
        }
        {
            var Q0;
            Q0=makeQuery(id+"F12.imprint","IMPRINT",FACE,{"disambiguationData":[TD([[makeQuery(id+"F12.imprint","IMPRINT",EDGE,{"derivedFrom":sQuery(id+"F12.wireOp",EDGE,"E36")}),-1.0]])]});
            extrude(context, id + "F13", {"entities" : qUnion([Q0]), "depth" : 15 * mm});
        }
        {
            var Q0;
            Q0=makeQuery(id+"F13.opExtrude","SWEPT_FACE",FACE,{"disambiguationData":[OSD([sQuery(id+"F12.wireOp",EDGE,"E41.2.1")])]});
            var sketch = newSketch(context, id + "F14", { "sketchPlane" : qUnion([Q0])});
            skCircle(sketch, "E59", {"center": v(27.75, 11.72) * mm, "radius": 2.1 * mm});
            skCircle(sketch, "E60", {"center": v(27.75, 4.72) * mm, "radius": 2.1 * mm});
            skSolve(sketch);
        }
        {
            var Q0;
            {var subQ0=makeQuery(id+"F13.opExtrude","SWEPT_EDGE",EDGE,{"disambiguationData":[OSD([sQuery(id+"F12.wireOp",EDGE,"E35"),sQuery(id+"F12.wireOp",EDGE,"E41.2.1")])]});var subQ1=sQuery(id+"F14.wireOp",EDGE,"E59");var subQ3=makeQuery(id+"F14.imprint","INTERSECT",VERTEX,{"disambiguationData":[OD(0.0)],"derivedFrom":[subQ0,subQ1]});Q0=makeQuery(id+"F14.imprint","IMPRINT",FACE,{"disambiguationData":[TD([[makeQuery(id+"F14.imprint","IMPRINT",EDGE,{"disambiguationData":[TD([[subQ3,1.0]])],"derivedFrom":subQ1}),1.0]])]});}
            var Q1;
            {var subQ0=sQuery(id+"F12.wireOp",EDGE,"E41.2.1");var subQ2=sQuery(id+"F14.wireOp",EDGE,"E60");var subQ5=makeQuery(id+"F13.opExtrude","SWEPT_EDGE",EDGE,{"disambiguationData":[OSD([sQuery(id+"F12.wireOp",EDGE,"E41.2.0"),subQ0])]});var subQ7=makeQuery(id+"F14.imprint","INTERSECT",VERTEX,{"disambiguationData":[OD(0.0)],"derivedFrom":[subQ5,subQ2]});Q1=makeQuery(id+"F14.imprint","IMPRINT",FACE,{"disambiguationData":[TD([[makeQuery(id+"F14.imprint","IMPRINT",EDGE,{"disambiguationData":[TD([[subQ7,-1.0]])],"derivedFrom":subQ2}),1.0]])]});}
            extrude(context, id + "F15", {"entities" : qUnion([Q0, Q1]), "oppositeDirection" : true, "depth" : 15 * mm});
        }
        {
            var Q0;
            Q0=makeQuery(id+"F15.opExtrude","SWEPT_BODY",BODY,{"disambiguationData":[OSD([sQuery(id+"F12.wireOp",EDGE,"E35"),sQuery(id+"F12.wireOp",EDGE,"E41.2.1"),sQuery(id+"F14.wireOp",EDGE,"E60")])]});
            var Q1;
            Q1=makeQuery(id+"F15.opExtrude","SWEPT_BODY",BODY,{"disambiguationData":[OSD([sQuery(id+"F12.wireOp",EDGE,"E35"),sQuery(id+"F12.wireOp",EDGE,"E41.2.1"),sQuery(id+"F14.wireOp",EDGE,"E59")])]});
            var Q2;
            Q2=makeQuery(id+"F13.opExtrude","CAP_EDGE",EDGE,{"disambiguationData":[OSD([sQuery(id+"F12.wireOp",EDGE,"E36")])],"isStart":false});
            circularPattern(context, id + "F16", {"entities" : qUnion([Q0, Q1]), "axis" : qUnion([Q2]), "angle" : 120 * degree, "instanceCount" : 3});
        }
        {
            var Q0;
            Q0=makeQuery(id+"F16.opPattern","COPY",BODY,{"derivedFrom":makeQuery(id+"F15.opExtrude","SWEPT_BODY",BODY,{"disambiguationData":[OSD([sQuery(id+"F12.wireOp",EDGE,"E35"),sQuery(id+"F12.wireOp",EDGE,"E41.2.1"),sQuery(id+"F14.wireOp",EDGE,"E59")])]}),"instanceName":"1"});
            var Q1;
            Q1=makeQuery(id+"F15.opExtrude","SWEPT_BODY",BODY,{"disambiguationData":[OSD([sQuery(id+"F12.wireOp",EDGE,"E35"),sQuery(id+"F12.wireOp",EDGE,"E41.2.1"),sQuery(id+"F14.wireOp",EDGE,"E59")])]});
            var Q2;
            Q2=makeQuery(id+"F15.opExtrude","SWEPT_BODY",BODY,{"disambiguationData":[OSD([sQuery(id+"F12.wireOp",EDGE,"E35"),sQuery(id+"F12.wireOp",EDGE,"E41.2.1"),sQuery(id+"F14.wireOp",EDGE,"E60")])]});
            var Q3;
            Q3=makeQuery(id+"F16.opPattern","COPY",BODY,{"derivedFrom":makeQuery(id+"F15.opExtrude","SWEPT_BODY",BODY,{"disambiguationData":[OSD([sQuery(id+"F12.wireOp",EDGE,"E35"),sQuery(id+"F12.wireOp",EDGE,"E41.2.1"),sQuery(id+"F14.wireOp",EDGE,"E60")])]}),"instanceName":"1"});
            var Q4;
            Q4=makeQuery(id+"F16.opPattern","COPY",BODY,{"derivedFrom":makeQuery(id+"F15.opExtrude","SWEPT_BODY",BODY,{"disambiguationData":[OSD([sQuery(id+"F12.wireOp",EDGE,"E35"),sQuery(id+"F12.wireOp",EDGE,"E41.2.1"),sQuery(id+"F14.wireOp",EDGE,"E59")])]}),"instanceName":"2"});
            var Q5;
            Q5=makeQuery(id+"F16.opPattern","COPY",BODY,{"derivedFrom":makeQuery(id+"F15.opExtrude","SWEPT_BODY",BODY,{"disambiguationData":[OSD([sQuery(id+"F12.wireOp",EDGE,"E35"),sQuery(id+"F12.wireOp",EDGE,"E41.2.1"),sQuery(id+"F14.wireOp",EDGE,"E60")])]}),"instanceName":"2"});
            var Q6;
            Q6=makeQuery(id+"F13.opExtrude","SWEPT_BODY",BODY,{"disambiguationData":[OSD([sQuery(id+"F12.wireOp",EDGE,"E35"),sQuery(id+"F12.wireOp",EDGE,"E36"),sQuery(id+"F12.wireOp",EDGE,"E39"),sQuery(id+"F12.wireOp",EDGE,"E40"),sQuery(id+"F12.wireOp",EDGE,"E41.1.0"),sQuery(id+"F12.wireOp",EDGE,"E41.1.1"),sQuery(id+"F12.wireOp",EDGE,"E41.2.0"),sQuery(id+"F12.wireOp",EDGE,"E41.2.1")])]});
            booleanBodies(context, id + "F17", {"operationType" : BooleanOperationType.SUBTRACTION, "tools" : qUnion([Q0, Q1, Q2, Q3, Q4, Q5]), "targets" : qUnion([Q6])});
        }
        {
            var Q0;
            Q0=makeQuery(id+"F12.imprint","IMPRINT",FACE,{"disambiguationData":[TD([[makeQuery(id+"F12.imprint","IMPRINT",EDGE,{"derivedFrom":sQuery(id+"F12.wireOp",EDGE,"E43")}),1.0]])]});
            extrude(context, id + "F18", {"entities" : qUnion([Q0]), "depth" : 20 * mm});
        }
        {
            var Q0;
            Q0=makeQuery(id+"F12.imprint","IMPRINT",FACE,{"disambiguationData":[TD([[makeQuery(id+"F12.imprint","IMPRINT",EDGE,{"derivedFrom":sQuery(id+"F12.wireOp",EDGE,"E51")}),1.0]])]});
            var Q1;
            {var subQ1=sQuery(id+"F12.wireOp",EDGE,"E58.1.0");Q1=makeQuery(id+"F12.imprint","IMPRINT",FACE,{"disambiguationData":[TD([[makeQuery(id+"F12.imprint","IMPRINT",EDGE,{"derivedFrom":subQ1}),-1.0]])]});}
            var Q2;
            {var subQ1=sQuery(id+"F12.wireOp",EDGE,"E58.2.0");Q2=makeQuery(id+"F12.imprint","IMPRINT",FACE,{"disambiguationData":[TD([[makeQuery(id+"F12.imprint","IMPRINT",EDGE,{"derivedFrom":subQ1}),-1.0]])]});}
            var Q3;
            {var subQ1=sQuery(id+"F12.wireOp",EDGE,"E58.3.0");Q3=makeQuery(id+"F12.imprint","IMPRINT",FACE,{"disambiguationData":[TD([[makeQuery(id+"F12.imprint","IMPRINT",EDGE,{"derivedFrom":subQ1}),-1.0]])]});}
            var Q4;
            {var subQ1=sQuery(id+"F12.wireOp",EDGE,"E58.4.0");Q4=makeQuery(id+"F12.imprint","IMPRINT",FACE,{"disambiguationData":[TD([[makeQuery(id+"F12.imprint","IMPRINT",EDGE,{"derivedFrom":subQ1}),-1.0]])]});}
            var Q5;
            {var subQ1=sQuery(id+"F12.wireOp",EDGE,"E58.5.0");Q5=makeQuery(id+"F12.imprint","IMPRINT",FACE,{"disambiguationData":[TD([[makeQuery(id+"F12.imprint","IMPRINT",EDGE,{"derivedFrom":subQ1}),-1.0]])]});}
            var Q6;
            {var subQ1=sQuery(id+"F12.wireOp",EDGE,"E54");Q6=makeQuery(id+"F12.imprint","IMPRINT",FACE,{"disambiguationData":[TD([[makeQuery(id+"F12.imprint","IMPRINT",EDGE,{"derivedFrom":subQ1}),1.0]])]});}
            extrude(context, id + "F19", {"entities" : qUnion([Q0, Q1, Q2, Q3, Q4, Q5, Q6]), "depth" : 25 * mm});
        }
        {
            var Q0;
            Q0=makeQuery(id+"F19.opExtrude","CAP_EDGE",EDGE,{"disambiguationData":[OSD([sQuery(id+"F12.wireOp",EDGE,"E54")])],"isStart":false});
            var Q1;
            Q1=makeQuery(id+"F19.opExtrude","CAP_EDGE",EDGE,{"disambiguationData":[OSD([sQuery(id+"F12.wireOp",EDGE,"E58.5.3")])],"isStart":false});
            var Q2;
            Q2=makeQuery(id+"F19.opExtrude","CAP_EDGE",EDGE,{"disambiguationData":[OSD([sQuery(id+"F12.wireOp",EDGE,"E58.1.3")])],"isStart":false});
            var Q3;
            Q3=makeQuery(id+"F19.opExtrude","CAP_EDGE",EDGE,{"disambiguationData":[OSD([sQuery(id+"F12.wireOp",EDGE,"E58.2.3")])],"isStart":false});
            var Q4;
            Q4=makeQuery(id+"F19.opExtrude","CAP_EDGE",EDGE,{"disambiguationData":[OSD([sQuery(id+"F12.wireOp",EDGE,"E58.3.3")])],"isStart":false});
            var Q5;
            Q5=makeQuery(id+"F19.opExtrude","CAP_EDGE",EDGE,{"disambiguationData":[OSD([sQuery(id+"F12.wireOp",EDGE,"E58.4.3")])],"isStart":false});
            var Q6;
            Q6=makeQuery(id+"F19.opExtrude","CAP_EDGE",EDGE,{"disambiguationData":[OSD([sQuery(id+"F12.wireOp",EDGE,"E58.1.3")])],"isStart":true});
            var Q7;
            Q7=makeQuery(id+"F19.opExtrude","CAP_EDGE",EDGE,{"disambiguationData":[OSD([sQuery(id+"F12.wireOp",EDGE,"E58.2.3")])],"isStart":true});
            var Q8;
            Q8=makeQuery(id+"F19.opExtrude","CAP_EDGE",EDGE,{"disambiguationData":[OSD([sQuery(id+"F12.wireOp",EDGE,"E54")])],"isStart":true});
            var Q9;
            Q9=makeQuery(id+"F19.opExtrude","CAP_EDGE",EDGE,{"disambiguationData":[OSD([sQuery(id+"F12.wireOp",EDGE,"E58.5.3")])],"isStart":true});
            var Q10;
            Q10=makeQuery(id+"F19.opExtrude","CAP_EDGE",EDGE,{"disambiguationData":[OSD([sQuery(id+"F12.wireOp",EDGE,"E58.4.3")])],"isStart":true});
            var Q11;
            Q11=makeQuery(id+"F19.opExtrude","CAP_EDGE",EDGE,{"disambiguationData":[OSD([sQuery(id+"F12.wireOp",EDGE,"E58.3.3")])],"isStart":true});
            fillet(context, id + "F20", {"entities" : qUnion([Q0, Q1, Q2, Q3, Q4, Q5, Q6, Q7, Q8, Q9, Q10, Q11]), "radius" : 0.5 * mm, "tangentPropagation" : true, "allowEdgeOverflow" : false});
        }
        {
            var Q0;
            Q0=makeQuery(id+"F12.imprint","IMPRINT",FACE,{"disambiguationData":[TD([[makeQuery(id+"F12.imprint","IMPRINT",EDGE,{"derivedFrom":sQuery(id+"F12.wireOp",EDGE,"E51")}),1.0]])]});
            var sketch = newSketch(context, id + "F21", { "sketchPlane" : qUnion([Q0])});
            skLineSegment(sketch, "E61.bottom", {"start": v(62.74, 35.82) * mm, "end": v(68.74, 35.82) * mm});
            skLineSegment(sketch, "E61.top", {"start": v(64.74, 30.96) * mm, "end": v(66.74, 30.96) * mm});
            skLineSegment(sketch, "E61.left", {"start": v(62.74, 35.82) * mm, "end": v(62.74, 32.96) * mm});
            skLineSegment(sketch, "E61.right", {"start": v(68.74, 35.82) * mm, "end": v(68.74, 32.96) * mm});
            skLineSegment(sketch, "E62", {"start": v(65.74, 30.96) * mm, "end": v(65.74, 42.03) * mm, "construction": true});
            skCircle(sketch, "E63", {"center": v(65.74, 33.96) * mm, "radius": 1.5 * mm});
            skPoint(sketch, "E64.visualSharp", {"position": v(62.74, 30.96) * mm});
            skArc(sketch, "E64.filletArc", {"start": v(62.74, 32.96) * mm, "mid": v(63.33, 31.55) * mm, "end": v(64.74, 30.96) * mm});
            skPoint(sketch, "E65.visualSharp", {"position": v(68.74, 30.96) * mm});
            skArc(sketch, "E65.filletArc", {"start": v(66.74, 30.96) * mm, "mid": v(68.16, 31.55) * mm, "end": v(68.74, 32.96) * mm});
            skSolve(sketch);
        }
        {
            var Q0;
            {var subQ8=sQuery(id+"F21.wireOp",EDGE,"E61.top");Q0=makeQuery(id+"F21.imprint","IMPRINT",FACE,{"disambiguationData":[TD([[makeQuery(id+"F21.imprint","IMPRINT",EDGE,{"derivedFrom":subQ8}),1.0]])]});}
            extrude(context, id + "F22", {"entities" : qUnion([Q0]), "operationType" : NewBodyOperationType.ADD, "depth" : 4 * mm});
        }
        {
            var Q0;
            {var subQ0=makeQuery(id+"F12.imprint","IMPRINT",EDGE,{"derivedFrom":sQuery(id+"F12.wireOp",EDGE,"E51")});var subQ1=sQuery(id+"F21.wireOp",EDGE,"E63");var subQ3=makeQuery(id+"F21.imprint","INTERSECT",VERTEX,{"disambiguationData":[OD(0.0)],"derivedFrom":[subQ0,subQ1]});Q0=makeQuery(id+"F21.imprint","IMPRINT",FACE,{"disambiguationData":[TD([[makeQuery(id+"F21.imprint","IMPRINT",EDGE,{"disambiguationData":[TD([[subQ3,-1.0]])],"derivedFrom":subQ1}),1.0]])]});}
            var Q1;
            {var subQ0=makeQuery(id+"F12.imprint","IMPRINT",EDGE,{"derivedFrom":sQuery(id+"F12.wireOp",EDGE,"E51")});var subQ1=sQuery(id+"F21.wireOp",EDGE,"E63");var subQ3=makeQuery(id+"F21.imprint","INTERSECT",VERTEX,{"disambiguationData":[OD(0.0)],"derivedFrom":[subQ0,subQ1]});Q1=makeQuery(id+"F21.imprint","IMPRINT",FACE,{"disambiguationData":[TD([[makeQuery(id+"F21.imprint","IMPRINT",EDGE,{"disambiguationData":[TD([[subQ3,1.0]])],"derivedFrom":subQ1}),1.0]])]});}
            extrude(context, id + "F23", {"entities" : qUnion([Q0, Q1]), "operationType" : NewBodyOperationType.REMOVE, "depth" : 9 * mm});
        }
    });
